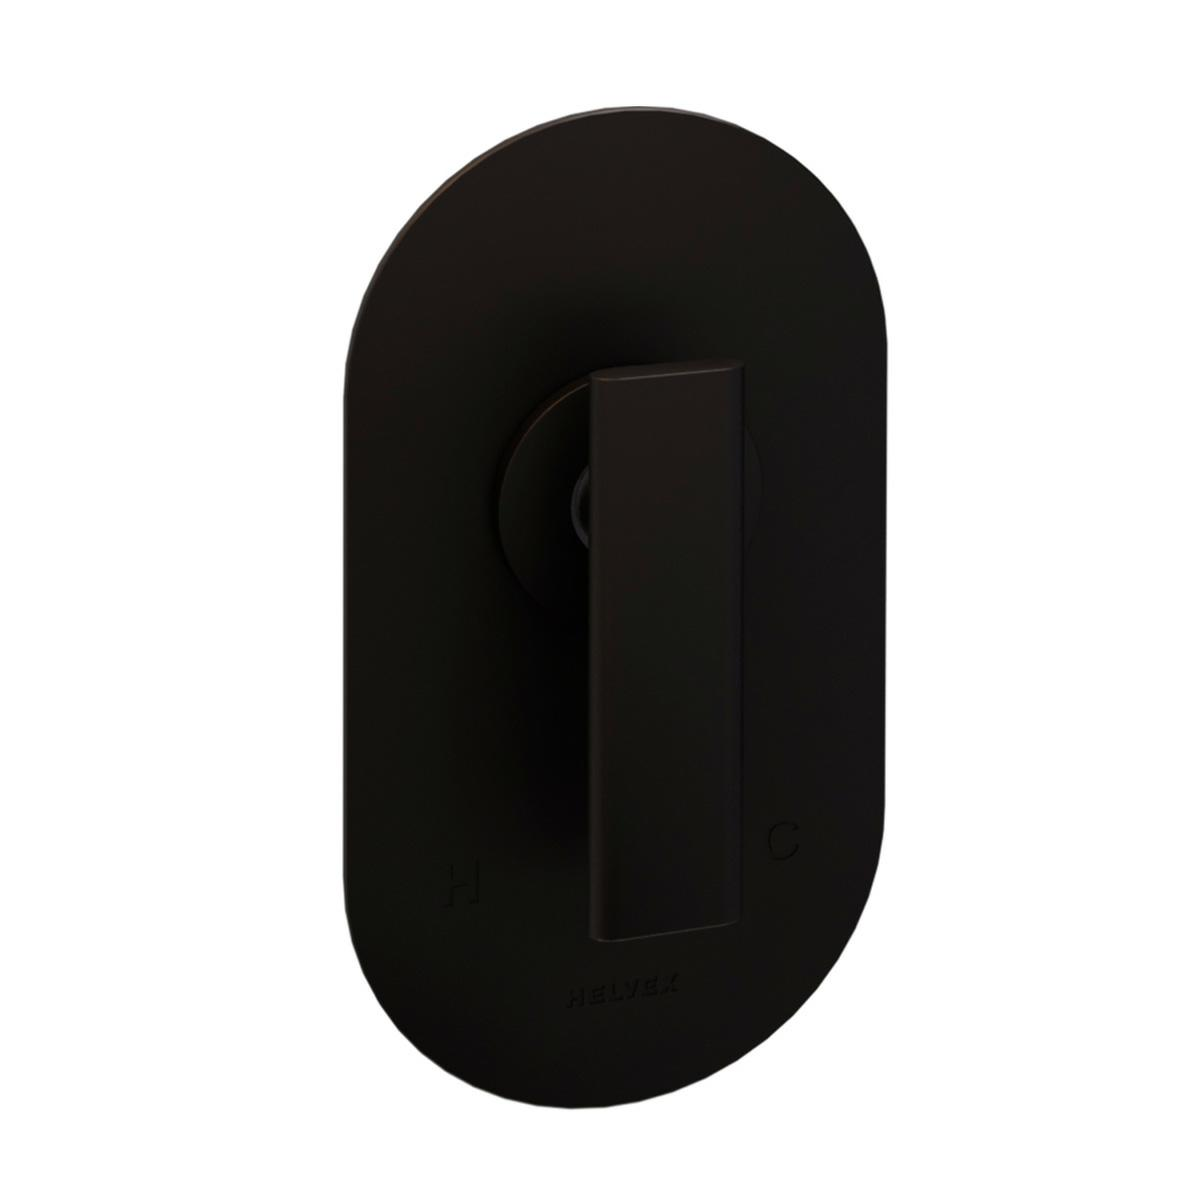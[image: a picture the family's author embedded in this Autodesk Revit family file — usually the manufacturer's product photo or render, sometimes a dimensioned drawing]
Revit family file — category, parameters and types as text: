
# Revit family: E-702-EB_RFA
name_source: partatom
category: Aparatos sanitarios
units: mm (PartAtom-declared; Revit-internal decimal feet)

## family parameters
Activar corte en vistas = No
Compartido = Sí
Corte con vacíos al cargar = No
Cota de conector redondo = Usar diámetro
Mantener orientación de anotación = No
Número OmniClass = 23.45.05.14.99
Punto de cálculo de habitación = Sí
Se basa en plano de trabajo = Sí
Siempre vertical = Sí
Tipo de pieza = Normal
Título OmniClass = Other Sanitary Washing Plumbing Fixtures

## types (1)
- E-702-EB
    Brass Chromed = Brass
    Cartucho = Cartucho monomando cerámico sin balanceo de presión Ø40mm
    Comentarios de tipo = Monomando para regadera o tina Premier Ébano
    Descripción = Monomando para regadera o tina Premier Ébano
    Elevación por defecto = 1"
    Fabricante = HELVEX S.A. DE C.V.
    Garantía = El producto HELVEX está garantizado como libre de defectos en materiales y procesos de fabricación. El producto HELVEX está garantizado, en lo que se refiere a los acabados; por un periodo de 10 años en los acabados cromo y duravex, y por 2 años en cabados diferentes al cromo, a partir de la fecha de compra indicada en la factura.
    Imagen de tipo = E-702-EB.jpg
    Instalación = ½" - 14 NPT
    Modelo = E-702-EB
    Operación = Para abrir el flujo de agua levante la palanca maneral y gire para regular la temperatura.
    Presión máxima de trabajo = 85.3 psi
    Presión mínima de trabajo = 11.4 psi
    Total Height = 7"
    Total Width = 4"
    URL = https://helvex.com.mx

## geometry (parser evidence)
native form markers: Sweep x3
no freeform markers — native parametric forms only
